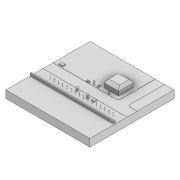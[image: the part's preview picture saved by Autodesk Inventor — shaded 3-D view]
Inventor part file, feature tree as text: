
AUTODESK INVENTOR PART (.ipt)
format: ipt  version: 2021 (Build 250183000, 183)  size: 279,552 bytes
history: native  units: in
note: dims shown in document units (in); Inventor stores cm internally (conversion verified against a paired STEP export)
features: extrude x10, sketch x10, projected_geometry x10, chamfer x2, plane x1, mirror x1, pattern_linear x1
ambient origin geometry x8: Origin, YZ Plane, XZ Plane, XY Plane, X Axis, Y Axis, Z Axis, Center Point
bodies: Solid1 (feature_tree)
feature tree (35):
  extrude  "Extrusion1"  Depth=3937.0079in
  extrude  "Extrusion2"  Depth=472.4409in
  extrude  "Extrusion3"  Depth=118.1102in
  extrude  "Extrusion4"  Depth=196.8504in TaperAngle=0.0deg
  extrude  "Extrusion5"  Depth=23.622in TaperAngle=0.0deg
  plane  "Work Plane1"
  mirror  "Mirror1"
  chamfer  "Chamfer1"  Distance=1.9685in Angle=45.0deg
  chamfer  "Chamfer2"  Distance=137.7953in Angle=45.0deg
  extrude  "Extrusion6"  Depth=118.1102in
  pattern_linear  "Rectangular Pattern1"  Count1=300 Spacing1=0.0in
  extrude  "Extrusion7"  Depth=118.1102in TaperAngle=0.0deg
  extrude  "Extrusion8"  Depth=118.1102in TaperAngle=0.0deg
  extrude  "Extrusion9"  [1 undecoded]
  extrude  "Extrusion10"  [1 undecoded]
  sketch  "Sketch1"  dims[d0=3937.0079in d1=3937.0079in]
  sketch  "Sketch2"  dims[d2=118.1102in d3=0.0in d4=472.4409in]
  projected_geometry  "Projected Loop1"
  sketch  "Sketch3"  dims[d5=433.0709in d6=118.1102in]
  projected_geometry  "Projected Loop2"
  projected_geometry  "Projected Loop3"
  sketch  "Sketch4"  dims[d7=3.937in d8=0.0in d9=196.8504in d10=0.0in]
  projected_geometry  "Projected Loop4"
  sketch  "Sketch5"  dims[d11=196.8504in d12=0.0in d13=23.622in d14=0.0in d15=1.9685in d16=0.125in d17=45.0deg d18=137.7953in d19=0.125in d20=45.0deg]
  projected_geometry  "Projected Loop5"
  sketch  "Sketch6"  dims[d21=19.685in d23=1479.4221in d24=118.1102in d25=0.0in]
  projected_geometry  "Projected Loop6"
  sketch  "Sketch7"  dims[d26=6.2992in d28=196.8504in d29=118.1102in d30=0.0in]
  projected_geometry  "Projected Loop7"
  sketch  "Sketch8"  dims[d31=39.3701in d32=0.0in d33=118.1102in d34=0.0in]
  projected_geometry  "Projected Loop8"
  projected_geometry  "Projected Loop9"
  sketch  "Sketch9"  dims[d35=236.1898in d36=0.0in]
  sketch  "Sketch10"
  projected_geometry  "Projected Loop10"
note: 2 required parameter values undecoded (feature->parameter linkage not recoverable at this tier; creation-order binding heuristic only, values carry confidence <= 0.55)
